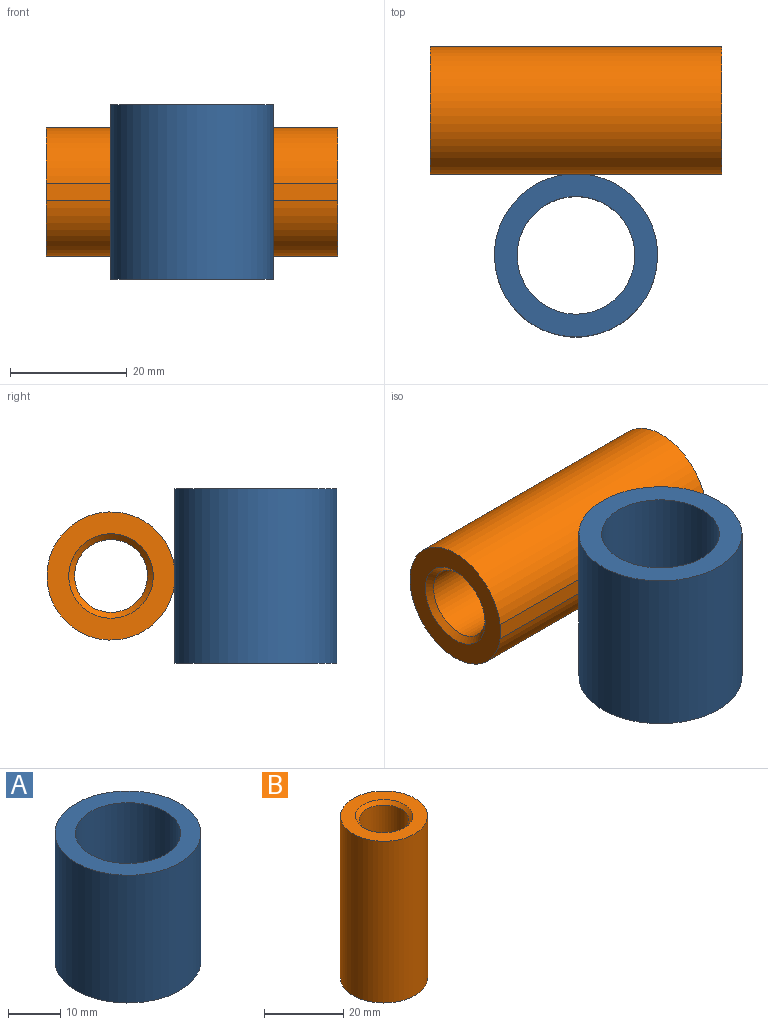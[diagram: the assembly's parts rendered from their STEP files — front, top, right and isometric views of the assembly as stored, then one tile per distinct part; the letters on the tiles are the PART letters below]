
ASSEMBLY  parts=2 mates=1
PART A: 5 faces, bbox 28x27.9x30 mm
  f0: cylinder r=10.1mm len=30mm, axis (0,0,-1), area 1903.8mm2, adj f2,f3
  f1: cylinder r=14mm len=30mm, axis (0,0,-1), area 2538.5mm2, adj f2,f3,f4
  f2: plane 28x27.9mm, normal (0,0,1), area 295.1mm2, adj f0,f1,f4
  f3: plane 28x27.9mm, normal (0,0,-1), area 295.1mm2, adj f0,f1,f4
  f4: plane 30x3.34mm, normal (0,1,0), area 100.2mm2, adj f1,f2,f3
PART B: 7 faces, bbox 22x21.9x50 mm
  f0: cylinder r=6.25mm len=48mm, axis (0,0,-1), area 1885mm2, adj f5,f6
  f1: cylinder r=11mm len=50mm, axis (0,0,-1), area 3307.3mm2, adj f2,f3,f4
  f2: plane 22x21.9mm, normal (0,0,1), area 214.8mm2, adj f1,f4,f5
  f3: plane 22x21.9mm, normal (0,0,-1), area 214.8mm2, adj f1,f4,f6
  f4: plane 50x2.96mm, normal (0,1,0), area 148mm2, adj f1,f2,f3
  f5: cone r=6.25mm half-angle=45deg, axis (0,0,1), area 60mm2, adj f0,f2
  f6: cone r=7.25mm half-angle=45deg, axis (0,0,-1), area 60mm2, adj f0,f3
PLACE A t=(-1.38,14.85,-1.61)mm
PLACE B rot(axis=(0.71,0,-0.71),180deg) t=(23.62,39.65,13.39)mm
MATE fastened B.f4 <-> A.f4  axis (0,-1,0) through (-1.38,28.75,13.39)mm
